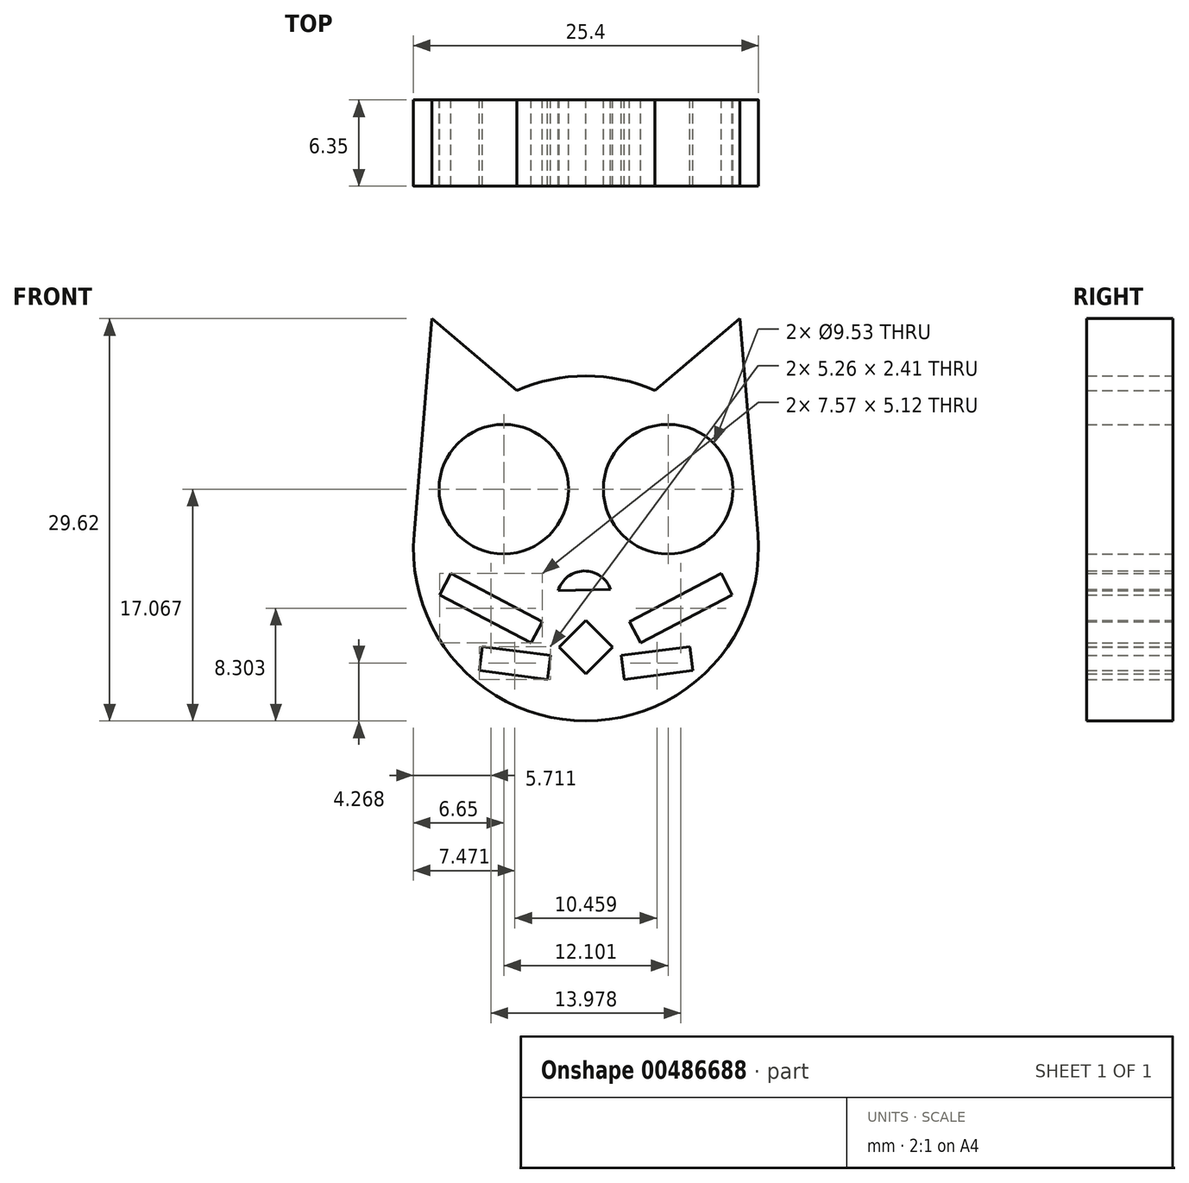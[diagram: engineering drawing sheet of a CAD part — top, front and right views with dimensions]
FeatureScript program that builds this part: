
annotation { "Feature Type Name" : "Feature", "Feature Type Description" : "" }
export const myFeature = defineFeature(function(context is Context, id is Id, definition is map)
    precondition{}
    {
        {
            var Q0;
            Q0=qCreatedBy(makeId("Front.planeOp"),FACE);
            var sketch = newSketch(context, id + "F0", { "sketchPlane" : qUnion([Q0])});
            skCircle(sketch, "E0", {"center": v(0, 0) * mm, "radius": 12.7 * mm});
            skCircle(sketch, "E1", {"center": v(6.05, 4.37) * mm, "radius": 4.76 * mm});
            skLineSegment(sketch, "E2.bottom", {"start": v(0, -5.28) * mm, "end": v(-1.98, -7.26) * mm});
            skLineSegment(sketch, "E2.top", {"start": v(1.98, -7.26) * mm, "end": v(0, -9.23) * mm});
            skLineSegment(sketch, "E2.left", {"start": v(0, -5.28) * mm, "end": v(1.98, -7.26) * mm});
            skLineSegment(sketch, "E2.right", {"start": v(-1.98, -7.26) * mm, "end": v(0, -9.23) * mm});
            skLineSegment(sketch, "E3.bottom", {"start": v(4.03, -6.95) * mm, "end": v(10.78, -3.41) * mm});
            skLineSegment(sketch, "E3.top", {"start": v(3.2, -5.38) * mm, "end": v(9.95, -1.84) * mm});
            skLineSegment(sketch, "E3.left", {"start": v(4.03, -6.95) * mm, "end": v(3.2, -5.38) * mm});
            skLineSegment(sketch, "E3.right", {"start": v(10.78, -3.41) * mm, "end": v(9.95, -1.84) * mm});
            skLineSegment(sketch, "E4.bottom", {"start": v(2.6, -7.87) * mm, "end": v(7.64, -7.23) * mm});
            skLineSegment(sketch, "E4.top", {"start": v(2.82, -9.64) * mm, "end": v(7.86, -9) * mm});
            skLineSegment(sketch, "E4.left", {"start": v(2.6, -7.87) * mm, "end": v(2.82, -9.64) * mm});
            skLineSegment(sketch, "E4.right", {"start": v(7.64, -7.23) * mm, "end": v(7.86, -9) * mm});
            skLineSegment(sketch, "E5", {"start": v(0, 76) * mm, "end": v(0, -78.53) * mm, "construction": true});
            skLineSegment(sketch, "E6.MirrorCS", {"start": v(-4.03, -6.95) * mm, "end": v(-3.2, -5.38) * mm});
            skLineSegment(sketch, "E7.MirrorCS", {"start": v(-10.78, -3.41) * mm, "end": v(-9.95, -1.84) * mm});
            skLineSegment(sketch, "E8.MirrorCS", {"start": v(-2.6, -7.87) * mm, "end": v(-2.82, -9.64) * mm});
            skLineSegment(sketch, "E9.MirrorCS", {"start": v(-7.64, -7.23) * mm, "end": v(-7.86, -9) * mm});
            skLineSegment(sketch, "E10.MirrorCS", {"start": v(-3.2, -5.38) * mm, "end": v(-9.95, -1.84) * mm});
            skLineSegment(sketch, "E11.MirrorCS", {"start": v(-2.82, -9.64) * mm, "end": v(-7.86, -9) * mm});
            skCircle(sketch, "E12.MirrorC", {"center": v(-6.05, 4.37) * mm, "radius": 4.76 * mm});
            skLineSegment(sketch, "E13.MirrorCS", {"start": v(-4.03, -6.95) * mm, "end": v(-10.78, -3.41) * mm});
            skLineSegment(sketch, "E14.MirrorCS", {"start": v(-2.6, -7.87) * mm, "end": v(-7.64, -7.23) * mm});
            skLineSegment(sketch, "E15", {"start": v(12.66, 1.05) * mm, "end": v(11.34, 16.92) * mm});
            skLineSegment(sketch, "E16", {"start": v(11.34, 16.92) * mm, "end": v(5.08, 11.64) * mm});
            skLineSegment(sketch, "E17.MirrorCS", {"start": v(-11.34, 16.92) * mm, "end": v(-5.08, 11.64) * mm});
            skLineSegment(sketch, "E18.MirrorCS", {"start": v(-12.66, 1.05) * mm, "end": v(-11.34, 16.92) * mm});
            skArc(sketch, "E19", {"start": v(1.81, -3) * mm, "mid": v(-0.15, -1.66) * mm, "end": v(-2.04, -3.1) * mm});
            skLineSegment(sketch, "E20", {"start": v(-2.04, -3.1) * mm, "end": v(1.81, -3) * mm});
            skPoint(sketch, "E21.orphan", {"position": v(0, 7.34) * mm});
            skSolve(sketch);
        }
        {
            var Q0;
            Q0 = qSketchRegion(id + "F0", true);
            extrude(context, id + "F1", {"entities" : qUnion([Q0]), "depth" : 6.35 * mm});
        }
    });
